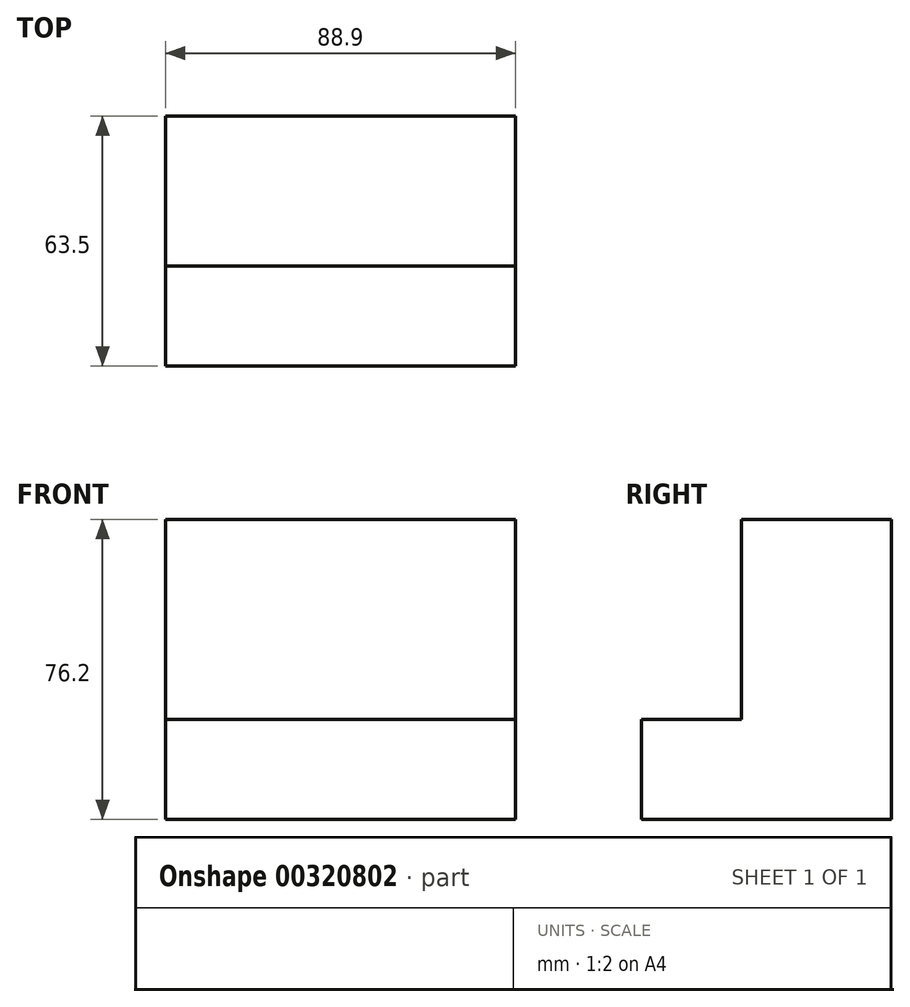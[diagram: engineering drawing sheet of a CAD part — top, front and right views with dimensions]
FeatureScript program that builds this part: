
annotation { "Feature Type Name" : "Feature", "Feature Type Description" : "" }
export const myFeature = defineFeature(function(context is Context, id is Id, definition is map)
    precondition{}
    {
        {
            var Q0;
            Q0=qCreatedBy(makeId("Right.planeOp"),FACE);
            var sketch = newSketch(context, id + "F0", { "sketchPlane" : qUnion([Q0])});
            skLineSegment(sketch, "E0", {"start": v(-15.22, -21.69) * mm, "end": v(-15.22, -47.09) * mm});
            skLineSegment(sketch, "E1", {"start": v(-15.22, -47.09) * mm, "end": v(48.28, -47.09) * mm});
            skLineSegment(sketch, "E2", {"start": v(48.28, -47.09) * mm, "end": v(48.28, 29.11) * mm});
            skLineSegment(sketch, "E3", {"start": v(48.28, 29.11) * mm, "end": v(10.18, 29.11) * mm});
            skLineSegment(sketch, "E4", {"start": v(10.18, 29.11) * mm, "end": v(10.18, -21.69) * mm});
            skLineSegment(sketch, "E5", {"start": v(10.18, -21.69) * mm, "end": v(-15.22, -21.69) * mm});
            skSolve(sketch);
        }
        {
            var Q0;
            Q0=makeQuery(id+"F0.imprint","IMPRINT",FACE,{"disambiguationData":[TD([[makeQuery(id+"F0.imprint","IMPRINT",EDGE,{"derivedFrom":sQuery(id+"F0.wireOp",EDGE,"E0")}),1.0]])]});
            extrude(context, id + "F1", {"entities" : qUnion([Q0]), "oppositeDirection" : true, "depth" : 88.9 * mm});
        }
    });
